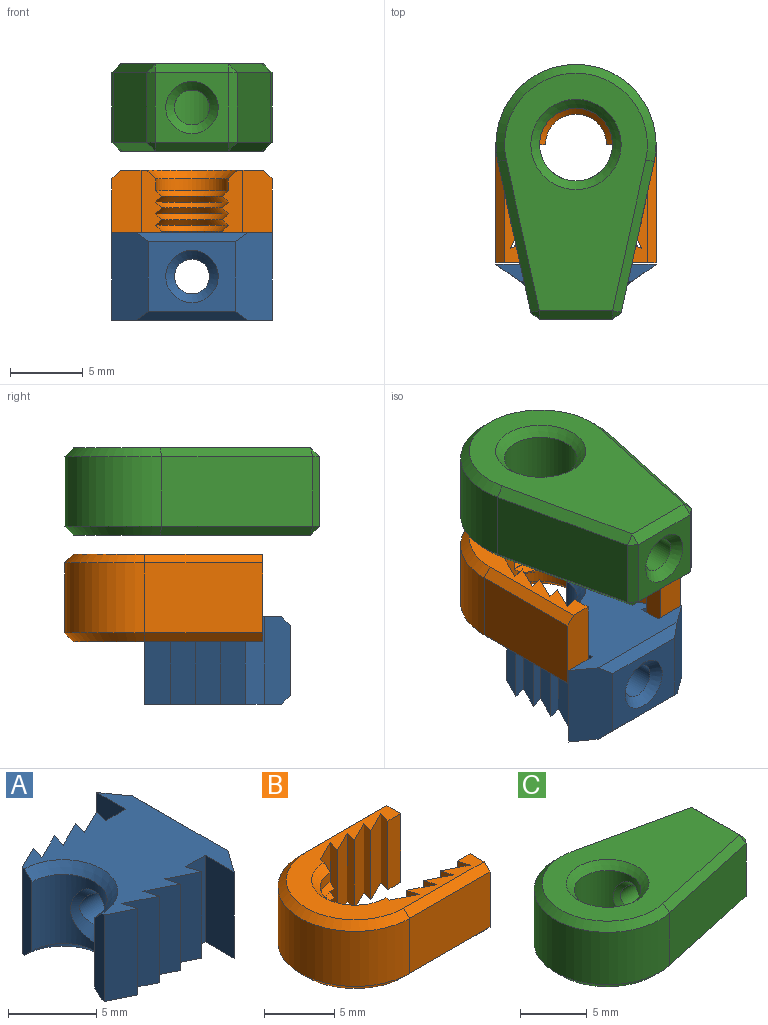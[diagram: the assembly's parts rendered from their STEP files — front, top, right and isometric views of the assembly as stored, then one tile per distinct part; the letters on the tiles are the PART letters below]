
ASSEMBLY  parts=3 mates=2
PART A: 35 faces, bbox 10x11x6 mm
  f0: plane 6x1mm, normal (0.96,0.29,0), area 6.3mm2, adj f1,f25,f26,f27
  f1: plane 6x2mm, normal (-0.45,-0.89,0), area 13.4mm2, adj f0,f2,f26,f27
  f2: plane 6x1mm, normal (0.96,0.29,0), area 6.3mm2, adj f1,f3,f26,f27
  f3: plane 6x2mm, normal (-0.45,-0.89,0), area 13.4mm2, adj f2,f4,f26,f27
  f4: plane 6x1mm, normal (0.96,0.29,0), area 6.3mm2, adj f3,f5,f26,f27
  f5: plane 6x2mm, normal (-0.45,-0.89,0), area 13.4mm2, adj f4,f6,f26,f27
  f6: plane 6x1mm, normal (0.96,0.29,0), area 6.3mm2, adj f5,f7,f26,f27
  f7: plane 6x1.6mm, normal (0,-1,0), area 9.6mm2, adj f6,f8,f26,f27
  f8: plane 6x2.3mm, normal (-1,0,0), area 13.8mm2, adj f7,f9,f26,f27
  f9: plane 6x2.5mm, normal (0.81,-0.58,0), area 17.9mm2, adj f8,f10,f26,f27,f31,f32
  f10: plane 6x4.8mm, normal (1,0,0), area 18.6mm2, adj f9,f11,f31,f32,f34
  f11: plane 6x2.5mm, normal (0.81,0.58,0), area 17.9mm2, adj f10,f12,f26,f27,f31,f32
  f12: plane 6x2.3mm, normal (-1,0,0), area 13.8mm2, adj f11,f13,f26,f27
  f13: plane 6x1.6mm, normal (0,1,0), area 9.6mm2, adj f12,f14,f26,f27
  f14: plane 6x1mm, normal (0.96,-0.29,0), area 6.3mm2, adj f13,f15,f26,f27
  f15: plane 6x2mm, normal (-0.45,0.89,0), area 13.4mm2, adj f14,f16,f26,f27
  f16: plane 6x1mm, normal (0.96,-0.29,0), area 6.3mm2, adj f15,f17,f26,f27
  f17: plane 6x2mm, normal (-0.45,0.89,0), area 13.4mm2, adj f16,f18,f26,f27
  f18: plane 6x1mm, normal (0.96,-0.29,0), area 6.3mm2, adj f17,f19,f26,f27
  f19: plane 6x2mm, normal (-0.45,0.89,0), area 13.4mm2, adj f18,f20,f26,f27
  f20: plane 6x1mm, normal (0.96,-0.29,0), area 6.3mm2, adj f19,f21,f26,f27
  f21: plane 6x1.8mm, normal (-0.45,0.89,0), area 12.1mm2, adj f20,f22,f26,f27
  f22: plane 6x0.8mm, normal (-1,0,0), area 4.4mm2, adj f21,f23,f26,f27,f29,f30
  f23: cylinder r=2.5mm len=5mm, axis (0,0,-1), area 29.1mm2, adj f22,f24,f29,f30,f33
  f24: plane 6x0.8mm, normal (-1,0,0), area 4.4mm2, adj f23,f25,f26,f27,f29,f30
  f25: plane 6x1.8mm, normal (-0.45,-0.89,0), area 12.1mm2, adj f0,f24,f26,f27
  f26: plane 11x9.4mm, normal (0,0,1), area 55.4mm2, adj f0,f1,f2,f3,f4,f5,f6,f7
  f27: plane 11x9.4mm, normal (0,0,-1), area 55.4mm2, adj f0,f1,f2,f3,f4,f5,f6,f7
  f28: cylinder r=1.2mm len=6.3mm, axis (1,0,0), area 47.5mm2, adj f33,f34
  f29: cone r=2.5mm half-angle=45deg, axis (0,0,1), area 7.5mm2, adj f22,f23,f24,f26
  f30: cone r=3.1mm half-angle=45deg, axis (0,0,-1), area 7.5mm2, adj f22,f23,f24,f27
  f31: plane 7.67x0.6mm, normal (0.71,0,-0.71), area 5.8mm2, adj f9,f10,f11,f27
  f32: plane 7.67x0.6mm, normal (0.71,0,0.71), area 5.8mm2, adj f9,f10,f11,f26
  f33: bspline ~3.6x2.9mm, area 6.4mm2, adj f23,f28
  f34: cone r=1.2mm half-angle=45deg, axis (1,0,0), area 8mm2, adj f10,f28
PART B: 45 faces, bbox 13.6x11x6 mm
  f0: cone r=2.5mm half-angle=45deg, axis (0,0,1), area 4.1mm2, adj f7,f8,f9,f10
  f1: cone r=2.1mm half-angle=45deg, axis (0,0,-1), area 4.1mm2, adj f2,f8,f10,f26
  f2: cone r=2.5mm half-angle=45deg, axis (0,0,1), area 4.1mm2, adj f1,f3,f8,f10
  f3: cone r=2.1mm half-angle=45deg, axis (0,0,-1), area 4.1mm2, adj f2,f4,f8,f10
  f4: cone r=2.5mm half-angle=45deg, axis (0,0,1), area 4.1mm2, adj f3,f5,f8,f10
  f5: cone r=2.1mm half-angle=45deg, axis (0,0,-1), area 4.1mm2, adj f4,f6,f8,f10
  f6: cone r=2.5mm half-angle=45deg, axis (0,0,1), area 4.1mm2, adj f5,f7,f8,f10
  f7: cone r=2.1mm half-angle=45deg, axis (0,0,-1), area 4.1mm2, adj f0,f6,f8,f10
  f8: plane 6x1.4mm, normal (1,0,0), area 6.3mm2, adj f0,f1,f2,f3,f4,f5,f6,f7
  f9: cylinder r=2.5mm len=5mm, axis (0,0,-1), area 6.3mm2, adj f0,f8,f10,f44
  f10: plane 6x1.4mm, normal (1,0,0), area 6.3mm2, adj f0,f1,f2,f3,f4,f5,f6,f7
  f11: plane 6x1.3mm, normal (0,-1,0), area 7.8mm2, adj f12,f34,f35,f36
  f12: plane 6x2mm, normal (1,0,0), area 11.6mm2, adj f11,f13,f35,f36,f37,f40
  f13: plane 8.1x4.8mm, normal (0,1,0), area 38.9mm2, adj f12,f14,f37,f40
  f14: cylinder r=5.5mm len=11mm, axis (0,0,-1), area 82.9mm2, adj f13,f15,f38,f41
  f15: plane 8.1x4.8mm, normal (0,-1,0), area 38.9mm2, adj f14,f16,f39,f42
  f16: plane 6x2mm, normal (1,0,0), area 11.6mm2, adj f15,f17,f35,f36,f39,f42
  f17: plane 6x1.3mm, normal (0,1,0), area 7.8mm2, adj f16,f18,f35,f36
  f18: plane 6x1mm, normal (-0.96,-0.29,0), area 6.3mm2, adj f17,f19,f35,f36
  f19: plane 6x2mm, normal (0.45,0.89,0), area 13.4mm2, adj f18,f20,f35,f36
  f20: plane 6x1mm, normal (-0.96,-0.29,0), area 6.3mm2, adj f19,f21,f35,f36
  f21: plane 6x2mm, normal (0.45,0.89,0), area 13.4mm2, adj f20,f22,f35,f36
  f22: plane 6x1mm, normal (-0.96,-0.29,0), area 6.3mm2, adj f21,f23,f35,f36
  f23: plane 6x2mm, normal (0.45,0.89,0), area 13.4mm2, adj f22,f24,f35,f36
  f24: plane 6x1mm, normal (-0.96,-0.29,0), area 6.3mm2, adj f23,f25,f35,f36
  f25: plane 6x2mm, normal (0.45,0.89,0), area 13.4mm2, adj f8,f24,f35,f36
  f26: cylinder r=2.5mm len=5mm, axis (0,0,-1), area 6.3mm2, adj f1,f8,f10,f43
  f27: plane 6x2mm, normal (0.45,-0.89,0), area 13.4mm2, adj f10,f28,f35,f36
  f28: plane 6x1mm, normal (-0.96,0.29,0), area 6.3mm2, adj f27,f29,f35,f36
  f29: plane 6x2mm, normal (0.45,-0.89,0), area 13.4mm2, adj f28,f30,f35,f36
  f30: plane 6x1mm, normal (-0.96,0.29,0), area 6.3mm2, adj f29,f31,f35,f36
  f31: plane 6x2mm, normal (0.45,-0.89,0), area 13.4mm2, adj f30,f32,f35,f36
  f32: plane 6x1mm, normal (-0.96,0.29,0), area 6.3mm2, adj f31,f33,f35,f36
  f33: plane 6x2mm, normal (0.45,-0.89,0), area 13.4mm2, adj f32,f34,f35,f36
  f34: plane 6x1mm, normal (-0.96,0.29,0), area 6.3mm2, adj f11,f33,f35,f36
  f35: plane 13x9.8mm, normal (0,0,1), area 38.5mm2, adj f8,f10,f11,f12,f16,f17,f18,f19
  f36: plane 13x9.8mm, normal (0,0,-1), area 38.5mm2, adj f8,f10,f11,f12,f16,f17,f18,f19
  f37: plane 8.1x0.6mm, normal (0,0.71,-0.71), area 6.9mm2, adj f12,f13,f36,f38
  f38: cone r=4.9mm half-angle=45deg, axis (0,0,1), area 13.9mm2, adj f14,f36,f37,f39
  f39: plane 8.1x0.6mm, normal (0,-0.71,-0.71), area 6.9mm2, adj f15,f16,f36,f38
  f40: plane 8.1x0.6mm, normal (0,0.71,0.71), area 6.9mm2, adj f12,f13,f35,f41
  f41: cone r=5.5mm half-angle=45deg, axis (0,0,-1), area 13.9mm2, adj f14,f35,f40,f42
  f42: plane 8.1x0.6mm, normal (0,-0.71,0.71), area 6.9mm2, adj f15,f16,f35,f41
  f43: cone r=2.5mm half-angle=45deg, axis (0,0,-1), area 7.5mm2, adj f8,f10,f26,f36
  f44: cone r=3.1mm half-angle=45deg, axis (0,0,1), area 7.5mm2, adj f8,f9,f10,f35
PART C: 26 faces, bbox 17.5x11x6 mm
  f0: plane 10.35x4.8mm, normal (0.21,0.98,0), area 50.9mm2, adj f1,f13,f18,f21
  f1: cylinder r=5.5mm len=11mm, axis (0,0,-1), area 94.3mm2, adj f0,f2,f10,f19
  f2: plane 10.35x4.8mm, normal (0.21,-0.98,0), area 50.9mm2, adj f1,f8,f11,f16
  f3: cylinder r=2.5mm len=5mm, axis (0,0,-1), area 66.8mm2, adj f22,f23,f24
  f4: plane 5.03x4.8mm, normal (1,0,0), area 14mm2, adj f11,f12,f17,f18,f25
  f5: plane 16.3x9.8mm, normal (0,0,1), area 93.3mm2, adj f8,f10,f12,f13,f23
  f6: plane 16.3x9.8mm, normal (0,0,-1), area 93.3mm2, adj f16,f17,f19,f21,f24
  f7: cylinder r=1.2mm len=8.3mm, axis (1,0,0), area 62.6mm2, adj f22,f25
  f8: plane 10.48x2.86mm, normal (0.15,-0.69,0.71), area 9mm2, adj f2,f5,f9,f10
  f9: plane 0.6x0.6mm, normal (0.61,-0.49,0.61), area 0.3mm2, adj f8,f11,f12
  f10: cone r=4.9mm half-angle=45deg, axis (0,0,-1), area 15.8mm2, adj f1,f5,f8,f13
  f11: plane 4.8x0.59mm, normal (0.78,-0.63,0), area 3.6mm2, adj f2,f4,f9,f14
  f12: plane 5.03x0.6mm, normal (0.71,0,0.71), area 4.3mm2, adj f4,f5,f9,f15
  f13: plane 10.48x2.86mm, normal (0.15,0.69,0.71), area 9mm2, adj f0,f5,f10,f15
  f14: plane 0.6x0.6mm, normal (0.61,-0.49,-0.61), area 0.3mm2, adj f11,f16,f17
  f15: plane 0.6x0.6mm, normal (0.61,0.49,0.61), area 0.3mm2, adj f12,f13,f18
  f16: plane 10.48x2.86mm, normal (0.15,-0.69,-0.71), area 9mm2, adj f2,f6,f14,f19
  f17: plane 5.03x0.6mm, normal (0.71,0,-0.71), area 4.3mm2, adj f4,f6,f14,f20
  f18: plane 4.8x0.59mm, normal (0.78,0.63,0), area 3.6mm2, adj f0,f4,f15,f20
  f19: cone r=5.5mm half-angle=45deg, axis (0,0,1), area 15.8mm2, adj f1,f6,f16,f21
  f20: plane 0.6x0.6mm, normal (0.61,0.49,-0.61), area 0.3mm2, adj f17,f18,f21
  f21: plane 10.48x2.86mm, normal (0.15,0.69,-0.71), area 9mm2, adj f0,f6,f19,f20
  f22: bspline ~3.6x2.9mm, area 6.4mm2, adj f3,f7
  f23: cone r=2.5mm half-angle=45deg, axis (0,0,1), area 14.9mm2, adj f3,f5
  f24: cone r=3.1mm half-angle=45deg, axis (0,0,-1), area 14.9mm2, adj f3,f6
  f25: cone r=1.2mm half-angle=45deg, axis (1,0,0), area 8mm2, adj f4,f7
PLACE A rot(axis=(-0.71,0.71,0),180deg) t=(3.09,7.06,-3.5)mm
PLACE B rot(axis=(0,0,-1),90deg) t=(3.09,7.06,0.8)mm
PLACE C rot(axis=(0,0,-1),90deg) t=(3.09,7.06,5.1)mm
MATE slider A.f23 <-> C.f3  axis (0,0,1) through (3.09,7.06,-3.5)mm
MATE slider A.f23 <-> B.f9  axis (0,0,1) through (3.09,7.06,-3.5)mm
